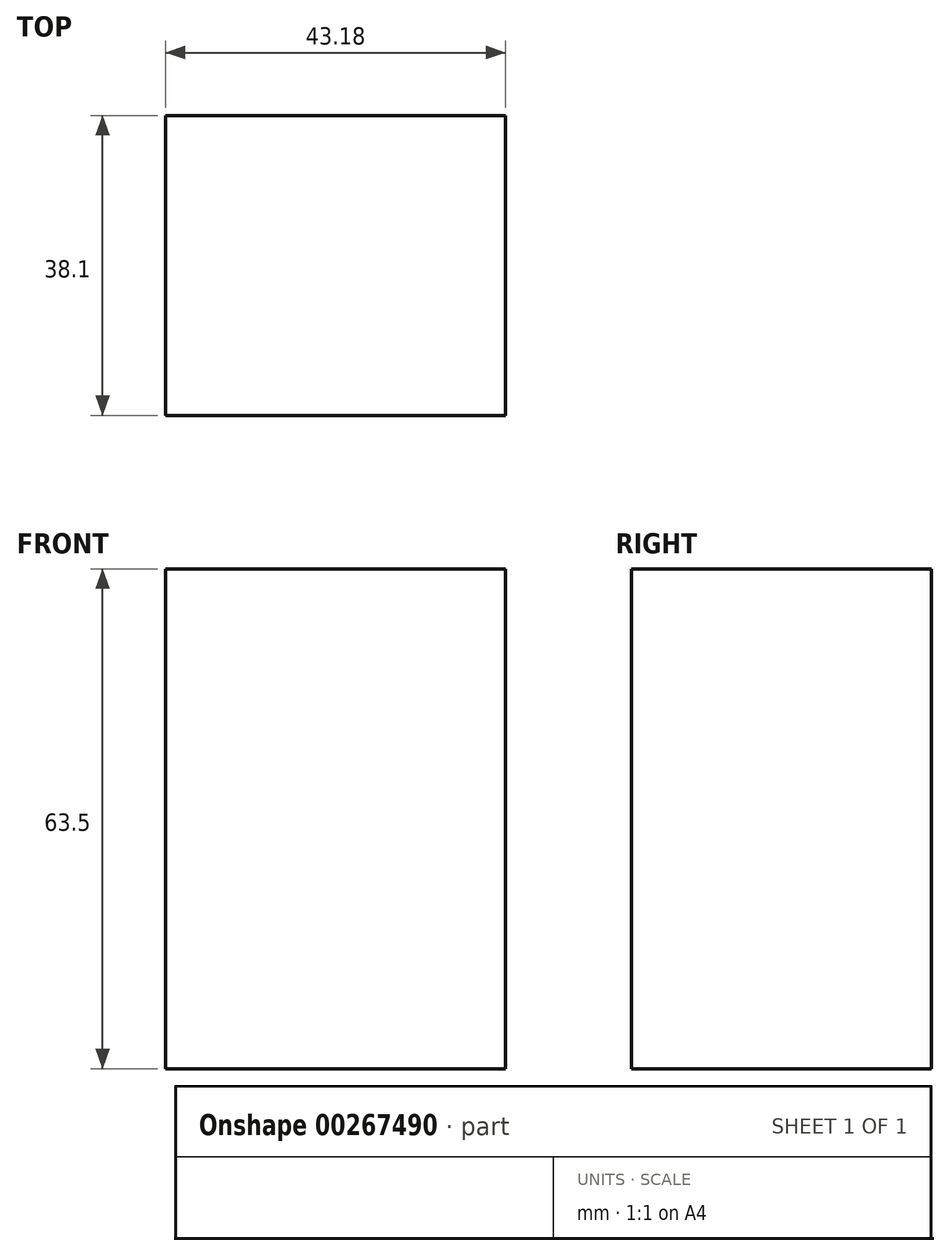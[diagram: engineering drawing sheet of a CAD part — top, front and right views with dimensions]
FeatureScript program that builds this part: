
annotation { "Feature Type Name" : "Feature", "Feature Type Description" : "" }
export const myFeature = defineFeature(function(context is Context, id is Id, definition is map)
    precondition{}
    {
        {
            var Q0;
            Q0=qCreatedBy(makeId("Front.planeOp"),FACE);
            var sketch = newSketch(context, id + "F0", { "sketchPlane" : qUnion([Q0])});
            skLineSegment(sketch, "E0.bottom", {"start": v(21.59, 31.75) * mm, "end": v(-21.6, 31.75) * mm});
            skLineSegment(sketch, "E0.top", {"start": v(21.6, -31.75) * mm, "end": v(-21.59, -31.75) * mm});
            skLineSegment(sketch, "E0.left", {"start": v(21.59, 31.75) * mm, "end": v(21.6, -31.75) * mm});
            skLineSegment(sketch, "E0.right", {"start": v(-21.6, 31.75) * mm, "end": v(-21.59, -31.75) * mm});
            skPoint(sketch, "E0.middle", {"position": v(0, 0) * mm});
            skSolve(sketch);
        }
        {
            var Q0;
            Q0 = qSketchRegion(id + "F0", true);
            extrude(context, id + "F1", {"entities" : qUnion([Q0]), "endBound" : BoundingType.SYMMETRIC, "depth" : 38.1 * mm});
        }
    });
